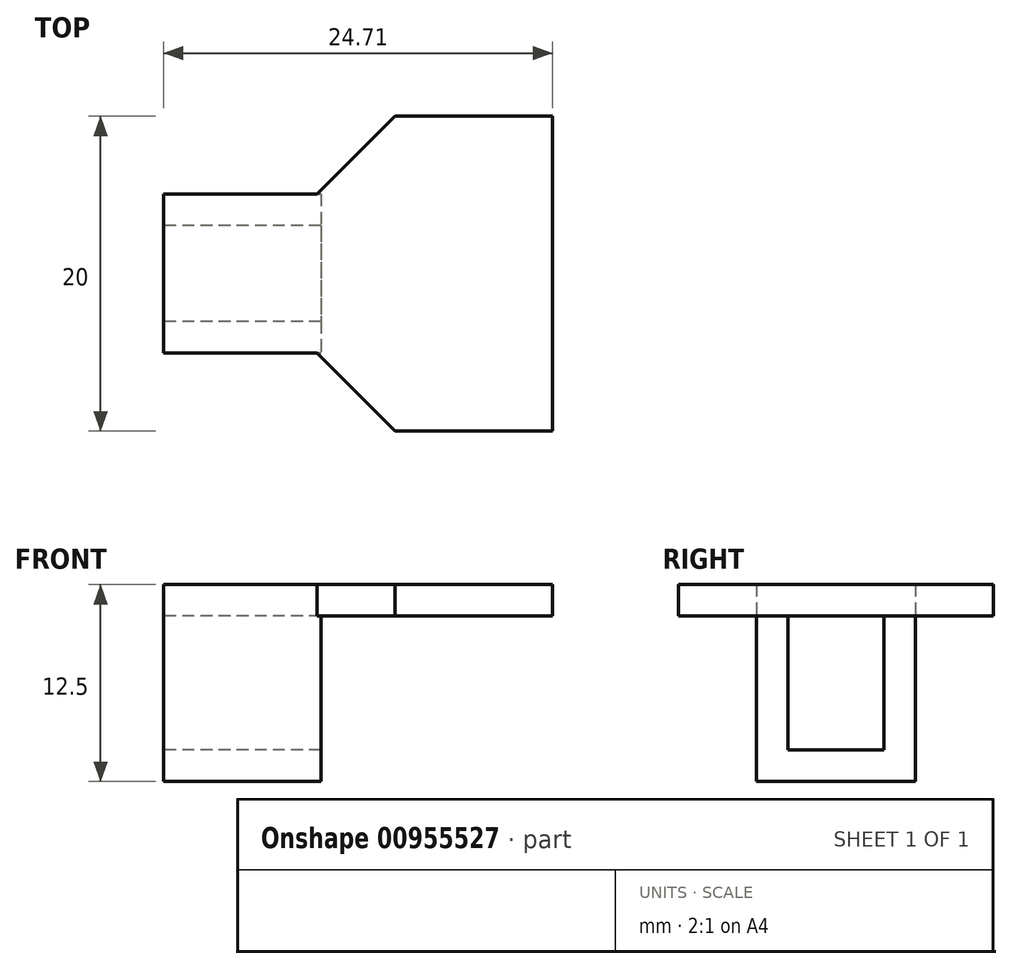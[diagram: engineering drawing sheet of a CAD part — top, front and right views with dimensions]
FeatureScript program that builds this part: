
annotation { "Feature Type Name" : "Feature", "Feature Type Description" : "" }
export const myFeature = defineFeature(function(context is Context, id is Id, definition is map)
    precondition{}
    {
        {
            var Q0;
            Q0=qCreatedBy(makeId("Right.planeOp"),FACE);
            var sketch = newSketch(context, id + "F0", { "sketchPlane" : qUnion([Q0])});
            skLineSegment(sketch, "E0.bottom", {"start": v(3.05, 4.25) * mm, "end": v(-3.05, 4.25) * mm});
            skLineSegment(sketch, "E0.top", {"start": v(3.05, -4.25) * mm, "end": v(-3.05, -4.25) * mm});
            skLineSegment(sketch, "E0.left", {"start": v(3.05, 4.25) * mm, "end": v(3.05, -4.25) * mm});
            skLineSegment(sketch, "E0.right", {"start": v(-3.05, 4.25) * mm, "end": v(-3.05, -4.25) * mm});
            skPoint(sketch, "E0.middle", {"position": v(0, 0) * mm});
            skLineSegment(sketch, "E1.bottom", {"start": v(5.05, 6.25) * mm, "end": v(-5.05, 6.25) * mm});
            skLineSegment(sketch, "E1.top", {"start": v(5.05, -6.25) * mm, "end": v(-5.05, -6.25) * mm});
            skLineSegment(sketch, "E1.left", {"start": v(5.05, 6.25) * mm, "end": v(5.05, -6.25) * mm});
            skLineSegment(sketch, "E1.right", {"start": v(-5.05, 6.25) * mm, "end": v(-5.05, -6.25) * mm});
            skSolve(sketch);
        }
        {
            var Q0;
            Q0=makeQuery(id+"F0.imprint","IMPRINT",FACE,{"disambiguationData":[TD([[makeQuery(id+"F0.imprint","IMPRINT",EDGE,{"derivedFrom":sQuery(id+"F0.wireOp",EDGE,"E0.bottom")}),-1.0]])]});
            var Q1;
            Q1=qConstructionFilter(qBodyType(qCreatedBy(id+"F0",EDGE),BodyType.WIRE),ConstructionObject.NO);
            extrude(context, id + "F1", {"entities" : qUnion([Q0]), "surfaceEntities" : qUnion([Q1]), "depth" : 10 * mm, "offsetDistance" : 25 * mm});
        }
        {
            var Q0;
            Q0=qCreatedBy(makeId("Front.planeOp"),FACE);
            var sketch = newSketch(context, id + "F2", { "sketchPlane" : qUnion([Q0])});
            skLineSegment(sketch, "E2", {"start": v(9.7, 4.25) * mm, "end": v(24.7, 4.25) * mm});
            skLineSegment(sketch, "E3", {"start": v(24.7, 4.25) * mm, "end": v(24.7, 4.25) * mm});
            skLineSegment(sketch, "E4", {"start": v(9.7, 4.25) * mm, "end": v(9.7, 6.25) * mm});
            skLineSegment(sketch, "E5", {"start": v(9.7, 6.25) * mm, "end": v(24.7, 6.25) * mm});
            skLineSegment(sketch, "E6", {"start": v(24.7, 6.25) * mm, "end": v(24.7, 4.25) * mm});
            skSolve(sketch);
        }
        {
            var Q0;
            Q0=qSketchRegion(id+"F2",true);
            extrude(context, id + "F3", {"entities" : qUnion([Q0]), "operationType" : NewBodyOperationType.ADD, "endBound" : BoundingType.SYMMETRIC, "depth" : 20 * mm, "offsetDistance" : 25 * mm});
        }
        {
            var Q0;
            Q0=makeQuery(id+"F3.opExtrude","CAP_EDGE",EDGE,{"disambiguationData":[OSD([sQuery(id+"F2.wireOp",EDGE,"E4")])],"isStart":true});
            var Q1;
            Q1=makeQuery(id+"F3.opExtrude","CAP_EDGE",EDGE,{"disambiguationData":[OSD([sQuery(id+"F2.wireOp",EDGE,"E4")])],"isStart":false});
            chamfer(context, id + "F4", {"entities" : qUnion([Q0, Q1]), "width" : 5 * mm, "tangentPropagation" : true});
        }
    });
